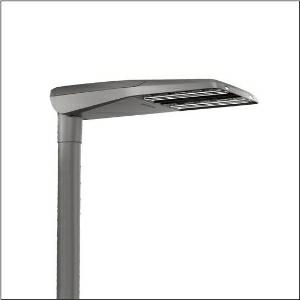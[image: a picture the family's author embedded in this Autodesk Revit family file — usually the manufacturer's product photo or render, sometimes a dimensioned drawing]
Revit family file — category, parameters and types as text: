
# Revit family: streetlight_sl_11_iq_midi___st1_2a_5xc3a51e08me_cf1e
name_source: partatom
category: Lighting Fixtures
units: mm (PartAtom-declared; Revit-internal decimal feet)

## family parameters
Cut with Voids When Loaded = No
Host = Face
Light Source = No
Part Type = Normal
Room Calculation Point = No
Round Connector Dimension = Use Diameter
Shared = No

## types (1)
- --- (1 x LED, 18110 lm, 124.7 W, 3000K)
    Apparent Load = 125 VA
    CIE Flux Codes = 32 70 96 100 100
    Color Rendering = 70
    Color Temperature = 3000K
    Default Elevation = 1800 mm
    Description = Streetlight SL 11 iQ midi, mast luminaire, primary light control with 3 zone facetted reflector, of plastic, silver coated, highly specular, primary optical cover: cover, of PMMA, transparent, light distribution: ST1.2a, light emission: direct distribution, primary light characteristic: asymmetric, installation type: post-top, side-entry, lamps: LED, High Power LED, rated values: 18.110lm | 124,7W | 145,2lm/W (begin service life); end service life: 18.110lm | 132,2W; at 50% lumin. flux: 9.055lm | 57,2W | 158,3lm/W, colour temperature: 3000K, colour rendering: CRI > 70, light colour: 730, light setting 1 begin service life: 100% | 18.110lm | 124,7W | 145,2lm/W | 3.000K, light setting 1 end service life: 132,2W, further light settings possible, control: optimised constant luminous flux control (CLO 2.0), Desk-Remote (wireless, voltage-free reading and setting of iQ features in the workshop via application-optimized NFC function/RFID function), Light-Fading, Smart-Wire, Night-Set, Lumen-Switch, Temp-Guard, Auto-Match, with cable H07RN-F 5x 1.5mm², mains connection: 230..240V, AC, 50/60Hz, connection cable pre-assembled, cable length: 12,5m, luminaire housing, of diecast aluminium, powder-coated, Siteco® metallic grey (DB 702S), please order mast flange separately, inclination adjustable without tools: 0°, 5°, 10°, 15° (post-top) | 0°, -5°, -10°, -15° (side-entry), sealing non-destructively replaceable, multi-level sealing system, length: 780mm, width: 376mm, height: 118mm, mast flange for spigot size: 42mm (side-entry): 5XC10008XM4, 60/48mm (side-entry/post-top): 5XC10108XM2, 76/60mm (side-entry/post-top): 5XC10108XM1, equipment: Power, protection rating (complete): IP66, insulation class (complete): insulation class II (safety insulation), certification: CE, ENEC, ENEC+, VDE, impact resistance: IK10, permissible operating ambient temperature for outdoor applications: -25..+50°C, standard-compliant lighting for roads and squares, Environmental Product Declaration (EPD) tested and certified by an independent institute, packaging unit: 1 piece

Light Distribution: ST1.2a
    Height = 118 mm
    Lamp = 1 x LED
    Lamp Light Flux = 18110 lm
    Lamp Power = 124.7 W
    Lamp count = 1
    Length = 780 mm
    Luminous efficacy = 145 lm/W
    Manufacturer = Siteco
    ModVariant = No
    Model = 5XC3A51E08ME
    Number of Poles = 1
    OnlyDefault = Yes
    Power Factor = 1
    Product Name = Streetlight SL 11 iQ midi | ST1.2a
    Product group = mast luminaire | pylon top
    ProductGroupID = 6100
    Protection Class = Protection class II
    Protection Degree = IP 66
    RLX_Detail_Level = 1
    RLX_Emergency_Light_Flux = 0 lm
    RLX_Emergency_Type = 0
    RLX_Emergency_Type_DB = No
    RlxData = <blob elided: 70997 chars, md5=bac8931e>
    Socket = socket
    Standby Power = 0 W
    System Light Flux = 18110 lm
    System Power = 125 W
    Type Comments = factory setting: luminous flux: 100 % | dim-lin: 254 | 557 mA
    Type Image = l_1005960.jpg
    URL = http://relux.com
    VarID = @adj_196258
    Voltage = 0 V
    Weight = 0.00 kg
    Width = 376 mm

## geometry (parser evidence)
native form markers: Blend x4, Sweep x10
no freeform markers — native parametric forms only
